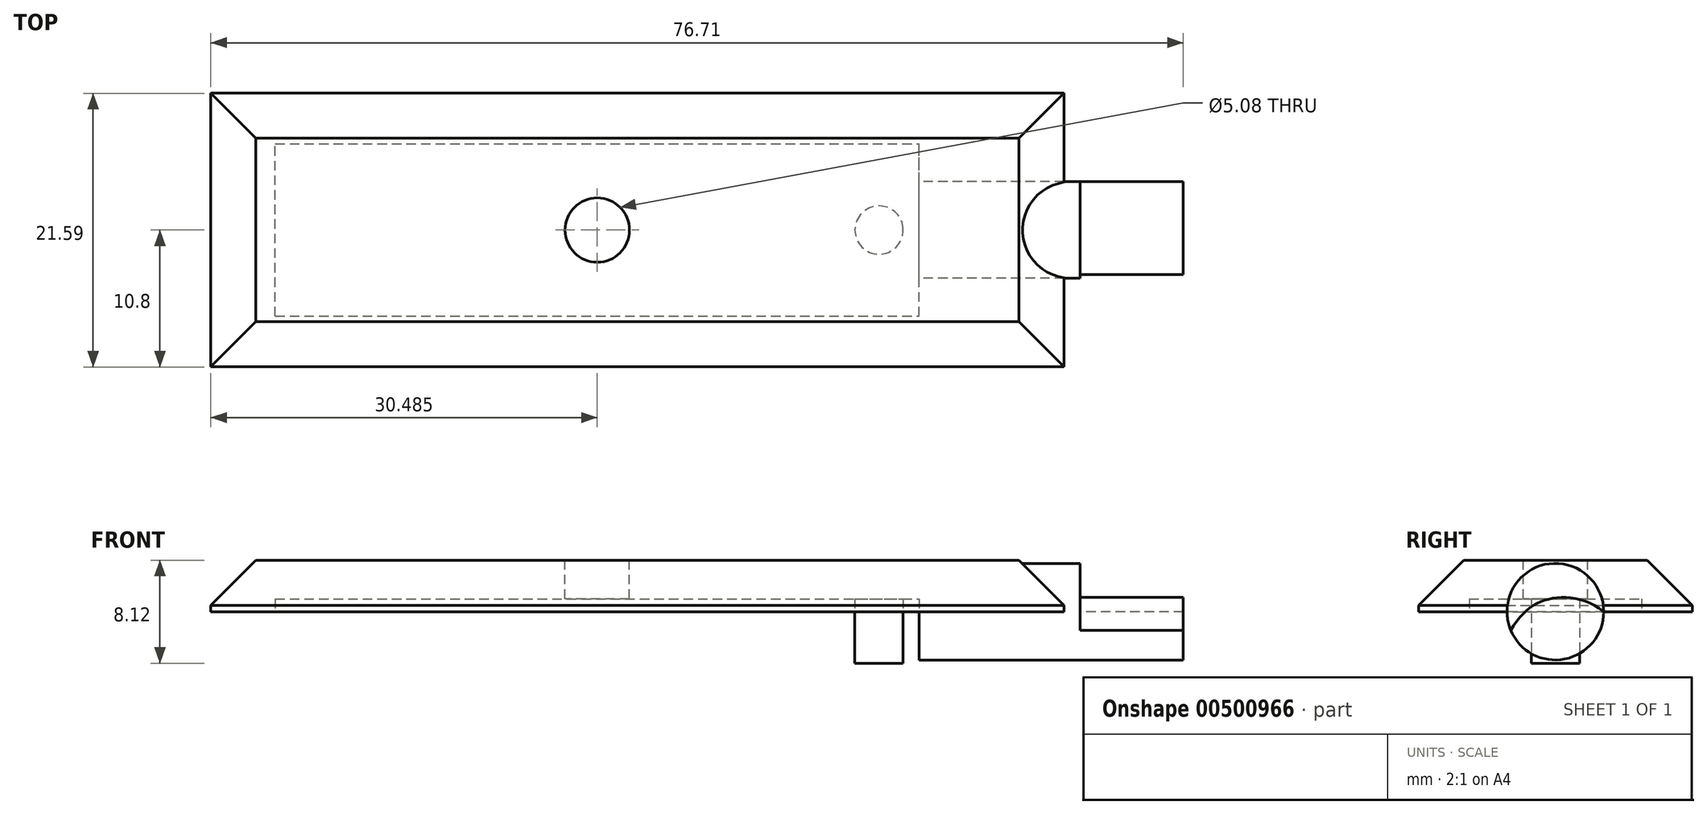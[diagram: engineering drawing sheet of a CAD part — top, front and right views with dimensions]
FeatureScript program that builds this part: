
annotation { "Feature Type Name" : "Feature", "Feature Type Description" : "" }
export const myFeature = defineFeature(function(context is Context, id is Id, definition is map)
    precondition{}
    {
        {
            var Q0;
            Q0=qCreatedBy(makeId("Top.planeOp"),FACE);
            var sketch = newSketch(context, id + "F0", { "sketchPlane" : qUnion([Q0])});
            skLineSegment(sketch, "E0.bottom", {"start": v(33.66, 10.8) * mm, "end": v(-33.66, 10.8) * mm});
            skLineSegment(sketch, "E0.top", {"start": v(33.66, -10.8) * mm, "end": v(-33.66, -10.8) * mm});
            skLineSegment(sketch, "E0.left", {"start": v(33.66, 10.8) * mm, "end": v(33.66, -10.8) * mm});
            skLineSegment(sketch, "E0.right", {"start": v(-33.66, 10.8) * mm, "end": v(-33.66, -10.8) * mm});
            skPoint(sketch, "E0.middle", {"position": v(0, 0) * mm});
            skSolve(sketch);
        }
        {
            var Q0;
            Q0=makeQuery(id+"F0.imprint","IMPRINT",FACE,{"disambiguationData":[TD([[makeQuery(id+"F0.imprint","IMPRINT",EDGE,{"derivedFrom":sQuery(id+"F0.wireOp",EDGE,"E0.bottom")}),1.0]])]});
            extrude(context, id + "F1", {"entities" : qUnion([Q0]), "depth" : 4.06 * mm});
        }
        {
            var Q0;
            Q0=makeQuery(id+"F1.opExtrude","CAP_FACE",FACE,{"disambiguationData":[OSD([sQuery(id+"F0.wireOp",EDGE,"E0.bottom"),sQuery(id+"F0.wireOp",EDGE,"E0.top"),sQuery(id+"F0.wireOp",EDGE,"E0.left"),sQuery(id+"F0.wireOp",EDGE,"E0.right")])],"isStart":false});
            var sketch = newSketch(context, id + "F2", { "sketchPlane" : qUnion([Q0])});
            skLineSegment(sketch, "E1", {"start": v(-33.66, 0) * mm, "end": v(-5.71, 0) * mm, "construction": true});
            skLineSegment(sketch, "E2", {"start": v(-5.71, 0) * mm, "end": v(-3.17, 0) * mm, "construction": true});
            skCircle(sketch, "E3", {"center": v(-3.17, 0) * mm, "radius": 2.54 * mm});
            skSolve(sketch);
        }
        {
            var Q0;
            Q0=makeQuery(id+"F1.opExtrude","CAP_EDGE",EDGE,{"disambiguationData":[OSD([sQuery(id+"F0.wireOp",EDGE,"E0.top")])],"isStart":false});
            var Q1;
            Q1=makeQuery(id+"F1.opExtrude","CAP_EDGE",EDGE,{"disambiguationData":[OSD([sQuery(id+"F0.wireOp",EDGE,"E0.right")])],"isStart":false});
            var Q2;
            Q2=makeQuery(id+"F1.opExtrude","CAP_EDGE",EDGE,{"disambiguationData":[OSD([sQuery(id+"F0.wireOp",EDGE,"E0.bottom")])],"isStart":false});
            var Q3;
            Q3=makeQuery(id+"F1.opExtrude","CAP_EDGE",EDGE,{"disambiguationData":[OSD([sQuery(id+"F0.wireOp",EDGE,"E0.left")])],"isStart":false});
            chamfer(context, id + "F3", {"entities" : qUnion([Q0, Q1, Q2, Q3]), "width" : 3.56 * mm, "tangentPropagation" : true});
        }
        {
            var Q0;
            Q0=makeQuery(id+"F2.imprint","IMPRINT",FACE,{"disambiguationData":[TD([[makeQuery(id+"F2.imprint","IMPRINT",EDGE,{"derivedFrom":sQuery(id+"F2.wireOp",EDGE,"E3")}),1.0]])]});
            var Q1;
            Q1=sQuery(id+"F2.wireOp",EDGE,"E3");
            extrude(context, id + "F4", {"entities" : qUnion([Q0]), "operationType" : NewBodyOperationType.REMOVE, "surfaceEntities" : qUnion([Q1]), "oppositeDirection" : true, "depth" : 25.4 * mm});
        }
        {
            var Q0;
            Q0=makeQuery(id+"F1.opExtrude","CAP_FACE",FACE,{"disambiguationData":[OSD([sQuery(id+"F0.wireOp",EDGE,"E0.bottom"),sQuery(id+"F0.wireOp",EDGE,"E0.top"),sQuery(id+"F0.wireOp",EDGE,"E0.left"),sQuery(id+"F0.wireOp",EDGE,"E0.right")])],"isStart":true});
            var sketch = newSketch(context, id + "F5", { "sketchPlane" : qUnion([Q0])});
            skLineSegment(sketch, "E4.bottom", {"start": v(-28.58, 6.8) * mm, "end": v(22.23, 6.8) * mm});
            skLineSegment(sketch, "E4.top", {"start": v(-28.57, -6.8) * mm, "end": v(22.22, -6.8) * mm});
            skLineSegment(sketch, "E4.left", {"start": v(-28.58, 6.8) * mm, "end": v(-28.58, -6.8) * mm});
            skLineSegment(sketch, "E4.right", {"start": v(22.23, 6.8) * mm, "end": v(22.23, -6.8) * mm});
            skPoint(sketch, "E4.middle", {"position": v(-3.17, 0) * mm});
            skSolve(sketch);
        }
        {
            var Q0;
            Q0=makeQuery(id+"F5.imprint","IMPRINT",FACE,{"disambiguationData":[TD([[makeQuery(id+"F5.imprint","IMPRINT",EDGE,{"derivedFrom":sQuery(id+"F5.wireOp",EDGE,"E4.bottom")}),-1.0]])]});
            extrude(context, id + "F6", {"entities" : qUnion([Q0]), "operationType" : NewBodyOperationType.ADD, "depth" : 4.06 * mm});
        }
        {
            var Q0;
            Q0=makeQuery(id+"F6.opExtrude","SWEPT_FACE",FACE,{"disambiguationData":[OSD([sQuery(id+"F5.wireOp",EDGE,"E4.right")])]});
            var sketch = newSketch(context, id + "F7", { "sketchPlane" : qUnion([Q0])});
            skCircle(sketch, "E5", {"center": v(0, 0) * mm, "radius": 3.81 * mm});
            skSolve(sketch);
        }
        {
            var Q0;
            {var subQ0=sQuery(id+"F7.wireOp",EDGE,"E5");var subQ1=makeQuery(id+"F6.opExtrude","CAP_EDGE",EDGE,{"disambiguationData":[OSD([sQuery(id+"F5.wireOp",EDGE,"E4.right")])],"isStart":true});var subQ2=makeQuery(id+"F7.imprint","INTERSECT",VERTEX,{"disambiguationData":[OD(0.0)],"derivedFrom":[subQ1,subQ0]});Q0=makeQuery(id+"F7.imprint","IMPRINT",FACE,{"disambiguationData":[TD([[makeQuery(id+"F7.imprint","IMPRINT",EDGE,{"disambiguationData":[TD([[subQ2,1.0]])],"derivedFrom":subQ0}),1.0]])]});}
            var Q1;
            {var subQ0=sQuery(id+"F7.wireOp",EDGE,"E5");var subQ1=makeQuery(id+"F6.opExtrude","CAP_EDGE",EDGE,{"disambiguationData":[OSD([sQuery(id+"F5.wireOp",EDGE,"E4.right")])],"isStart":true});var subQ2=makeQuery(id+"F7.imprint","INTERSECT",VERTEX,{"disambiguationData":[OD(0.0)],"derivedFrom":[subQ1,subQ0]});Q1=makeQuery(id+"F7.imprint","IMPRINT",FACE,{"disambiguationData":[TD([[makeQuery(id+"F7.imprint","IMPRINT",EDGE,{"disambiguationData":[TD([[subQ2,-1.0]])],"derivedFrom":subQ0}),1.0]])]});}
            extrude(context, id + "F8", {"entities" : qUnion([Q0, Q1]), "operationType" : NewBodyOperationType.ADD, "depth" : 12.7 * mm});
        }
        {
            var Q0;
            Q0=makeQuery(id+"F6.opExtrude","CAP_FACE",FACE,{"disambiguationData":[OSD([sQuery(id+"F0.wireOp",EDGE,"E0.bottom"),sQuery(id+"F0.wireOp",EDGE,"E0.top"),sQuery(id+"F0.wireOp",EDGE,"E0.left"),sQuery(id+"F0.wireOp",EDGE,"E0.right"),sQuery(id+"F2.wireOp",EDGE,"E3"),sQuery(id+"F5.wireOp",EDGE,"E4.bottom"),sQuery(id+"F5.wireOp",EDGE,"E4.top"),sQuery(id+"F5.wireOp",EDGE,"E4.left"),sQuery(id+"F5.wireOp",EDGE,"E4.right")])],"isStart":false});
            var sketch = newSketch(context, id + "F9", { "sketchPlane" : qUnion([Q0])});
            skLineSegment(sketch, "E6", {"start": v(-28.58, 0) * mm, "end": v(-25.4, 0) * mm, "construction": true});
            skPoint(sketch, "E6.endSnap0", {"position": v(-28.58, 0) * mm});
            skCircle(sketch, "E7", {"center": v(-25.4, 0) * mm, "radius": 1.9 * mm});
            skLineSegment(sketch, "E8", {"start": v(-3.17, 6.8) * mm, "end": v(-3.17, -6.8) * mm, "construction": true});
            skCircle(sketch, "E9.MirrorC", {"center": v(19.05, 0) * mm, "radius": 1.9 * mm});
            skSolve(sketch);
        }
        {
            var Q0;
            Q0=makeQuery(id+"F9.imprint","IMPRINT",FACE,{"disambiguationData":[TD([[makeQuery(id+"F9.imprint","IMPRINT",EDGE,{"derivedFrom":sQuery(id+"F9.wireOp",EDGE,"E7")}),1.0]])]});
            var Q1;
            Q1=makeQuery(id+"F9.imprint","IMPRINT",FACE,{"disambiguationData":[TD([[makeQuery(id+"F9.imprint","IMPRINT",EDGE,{"derivedFrom":sQuery(id+"F9.wireOp",EDGE,"E9.MirrorC")}),-1.0]])]});
            extrude(context, id + "F10", {"entities" : qUnion([Q0, Q1]), "operationType" : NewBodyOperationType.REMOVE, "oppositeDirection" : true, "depth" : 5.08 * mm});
        }
        {
            var Q0;
            Q0=makeQuery(id+"F8.opExtrude","CAP_FACE",FACE,{"disambiguationData":[OSD([sQuery(id+"F7.wireOp",EDGE,"E5")])],"isStart":false});
            var sketch = newSketch(context, id + "F11", { "sketchPlane" : qUnion([Q0])});
            skCircle(sketch, "E10", {"center": v(0, 0) * mm, "radius": 3.81 * mm});
            skPoint(sketch, "E11", {"position": v(1.56, -3.48) * mm});
            skPoint(sketch, "E12", {"position": v(-3.52, -1.47) * mm});
            skPoint(sketch, "E13", {"position": v(3.81, 0) * mm});
            skPoint(sketch, "E14", {"position": v(-0.5, 1) * mm});
            skFitSpline(sketch, "E15", {"points": [v(-3.52, -1.47) * mm, v(-0.5, 1) * mm, v(3.81, 0) * mm], "startDerivative": vector(5.39, 9.07) * mm, "endDerivative": vector(8.25, -6.57) * mm});
            skArc(sketch, "E16", {"start": v(-3.52, -1.47) * mm, "mid": v(0.75, -3.74) * mm, "end": v(3.81, 0) * mm});
            skSolve(sketch);
        }
        {
            var Q0;
            {var subQ0=sQuery(id+"F11.wireOp",EDGE,"E15");var subQ1=sQuery(id+"F11.wireOp",EDGE,"E10");var subQ2=makeQuery(id+"F11.imprint","INTERSECT",VERTEX,{"disambiguationData":[OD(0.0)],"derivedFrom":[subQ1,subQ0]});Q0=makeQuery(id+"F11.imprint","IMPRINT",FACE,{"disambiguationData":[TD([[makeQuery(id+"F11.imprint","IMPRINT",EDGE,{"disambiguationData":[TD([[subQ2,-1.0]])],"derivedFrom":subQ1}),1.0]])]});}
            extrude(context, id + "F12", {"entities" : qUnion([Q0]), "operationType" : NewBodyOperationType.ADD, "depth" : 8.13 * mm});
        }
    });
